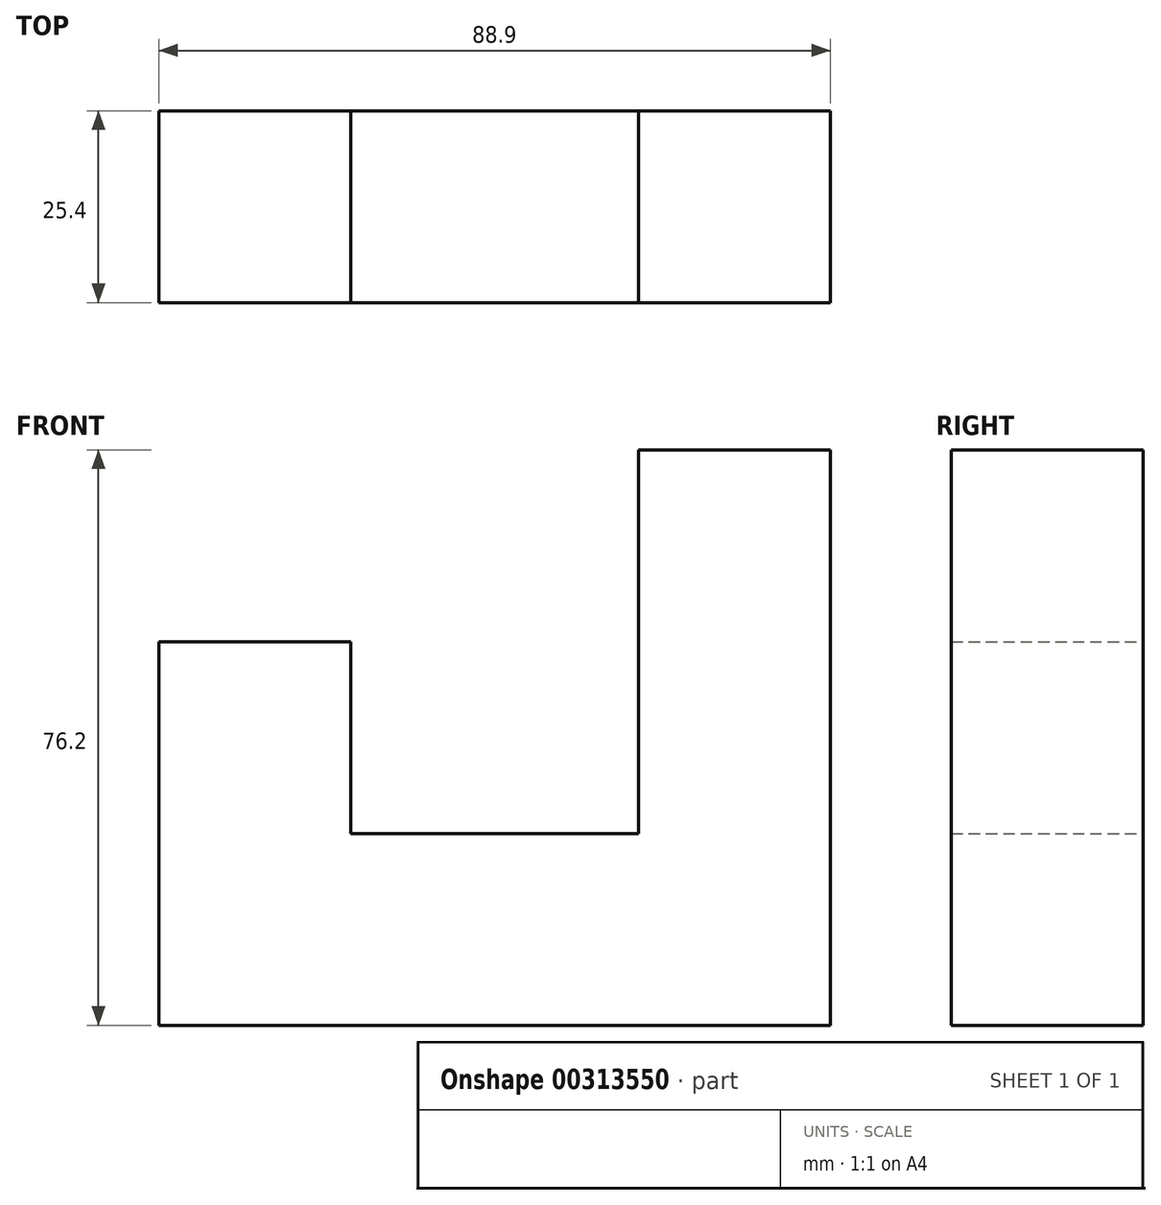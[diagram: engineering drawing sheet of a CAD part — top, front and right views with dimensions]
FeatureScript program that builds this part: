
annotation { "Feature Type Name" : "Feature", "Feature Type Description" : "" }
export const myFeature = defineFeature(function(context is Context, id is Id, definition is map)
    precondition{}
    {
        {
            var Q0;
            Q0=qCreatedBy(makeId("Front.planeOp"),FACE);
            var sketch = newSketch(context, id + "F0", { "sketchPlane" : qUnion([Q0])});
            skLineSegment(sketch, "E0", {"start": v(-44.05, -46.3) * mm, "end": v(44.85, -46.3) * mm});
            skLineSegment(sketch, "E1", {"start": v(44.85, -46.3) * mm, "end": v(44.85, 29.9) * mm});
            skLineSegment(sketch, "E2", {"start": v(44.85, 29.9) * mm, "end": v(19.45, 29.9) * mm});
            skLineSegment(sketch, "E3", {"start": v(19.45, 29.9) * mm, "end": v(19.45, -20.9) * mm});
            skLineSegment(sketch, "E4", {"start": v(19.45, -20.9) * mm, "end": v(-18.65, -20.9) * mm});
            skLineSegment(sketch, "E5", {"start": v(-18.65, -20.9) * mm, "end": v(-18.65, 4.5) * mm});
            skLineSegment(sketch, "E6", {"start": v(-44.05, -46.3) * mm, "end": v(-44.05, 4.5) * mm});
            skLineSegment(sketch, "E7", {"start": v(-44.05, 4.5) * mm, "end": v(-18.65, 4.5) * mm});
            skSolve(sketch);
        }
        {
            var Q0;
            Q0=makeQuery(id+"F0.imprint","IMPRINT",FACE,{"disambiguationData":[TD([[makeQuery(id+"F0.imprint","IMPRINT",EDGE,{"derivedFrom":sQuery(id+"F0.wireOp",EDGE,"E0")}),1.0]])]});
            extrude(context, id + "F1", {"entities" : qUnion([Q0]), "depth" : 25.4 * mm});
        }
    });
